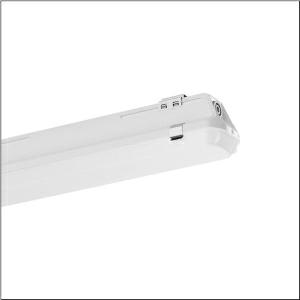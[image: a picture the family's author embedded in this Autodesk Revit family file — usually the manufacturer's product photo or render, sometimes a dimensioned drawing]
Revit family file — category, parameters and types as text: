
# Revit family: monsun_r__11_51fp10mp480h_5fdf
name_source: partatom
category: Lighting Fixtures
units: mm (PartAtom-declared; Revit-internal decimal feet)

## family parameters
Cut with Voids When Loaded = No
Host = Face
Light Source = No
Part Type = Normal
Room Calculation Point = No
Round Connector Dimension = Use Diameter
Shared = No

## types (1)
- --- (1 x LED, 8070 lm, 45.4 W, 4000K)
    Apparent Load = 45 VA
    CIE Flux Codes = 47 77 93 94 100
    Color Rendering = 80
    Color Temperature = 4000K
    Default Elevation = 1800 mm
    Description = Monsun® 11, damp-proof luminaire, chain hanger, primary optical cover: enclosure, of PMMA, light emission: direct distribution, primary light characteristic: symmetric, installation type: suspended mounting, surface-mounted, horizontal mounting, vertical mounting, LED, rated luminous flux: 8.070lm, luminous efficacy: 178lm/W, light colour: 840, colour temperature: 4000K, control gear: ECG, with terminal, 3-pole, max. 2.5mm², mains connection: 220..240V, AC, 50/60Hz, rated input power: 45W, luminaire housing, of glass-fibre reinforced polyester, uncoated, bright grey, incl. chain hanger, length: 1.590mm, width: 90mm, height: 88mm, clip for enclosure, of stainless steel (V2A), ceiling mounting element, of stainless steel (V2A), chain hanger, of stainless steel (V2A), protection rating (complete): IP66, insulation class (complete): insulation class I (protective earthing), certification: CE, ENEC, VDE, UKCA, protection symbol: D, impact resistance: IK04, permissible operating ambient temperature: -35..+40°C, standard: EN 50419, EN 60598-2-1, no direct snow, no direct sun, no direct rain, for indoor or canopied outdoor use, corresponds to IFS (International Featured Standards) requirements for safety and quality in the food industry, contact your sales advisor before using the luminaires in applications with unclear chemical exposure, large temperature fluctuations or condensation-forming humidity, LABS conformity tested according to VDMA 24364:2018-05, packaging unit: 1 piece
    Height = 89 mm
    Lamp = 1 x LED
    Lamp Light Flux = 8070 lm
    Lamp Power = 45.4 W
    Lamp count = 1
    Length = 1590 mm
    Luminous efficacy = 178 lm/W
    Manufacturer = Siteco
    ModVariant = No
    Model = 51FP10MP480H
    Mounting Place = Ceiling
    Mounting Type = Surface mounted
    Number of Poles = 1
    OnlyDefault = Yes
    Power Factor = 1
    Product Name = Monsun® 11
    Product group = damp-proof luminaire
    ProductGroupID = 300
    Protection Class = Protection class I
    Protection Degree = IP 66
    RLX_Detail_Level = 1
    RLX_Emergency_Light_Flux = 0 lm
    RLX_Emergency_Type = 0
    RLX_Emergency_Type_DB = No
    RlxData = <blob elided: 89913 chars, md5=a53b3396>
    Socket = socket
    Standby Power = 0 W
    System Light Flux = 8070 lm
    System Power = 45 W
    Type Comments = factory setting: luminous flux: 100 % | (A | C | E) | 105 mA
    Type Image = l_1319650.jpg
    URL = http://relux.com
    VarID = @adj_174983
    Voltage = 0 V
    Weight = 0.00 kg
    Width = 90 mm

## geometry (parser evidence)
native form markers: Blend x4, Sweep x13
no freeform markers — native parametric forms only
